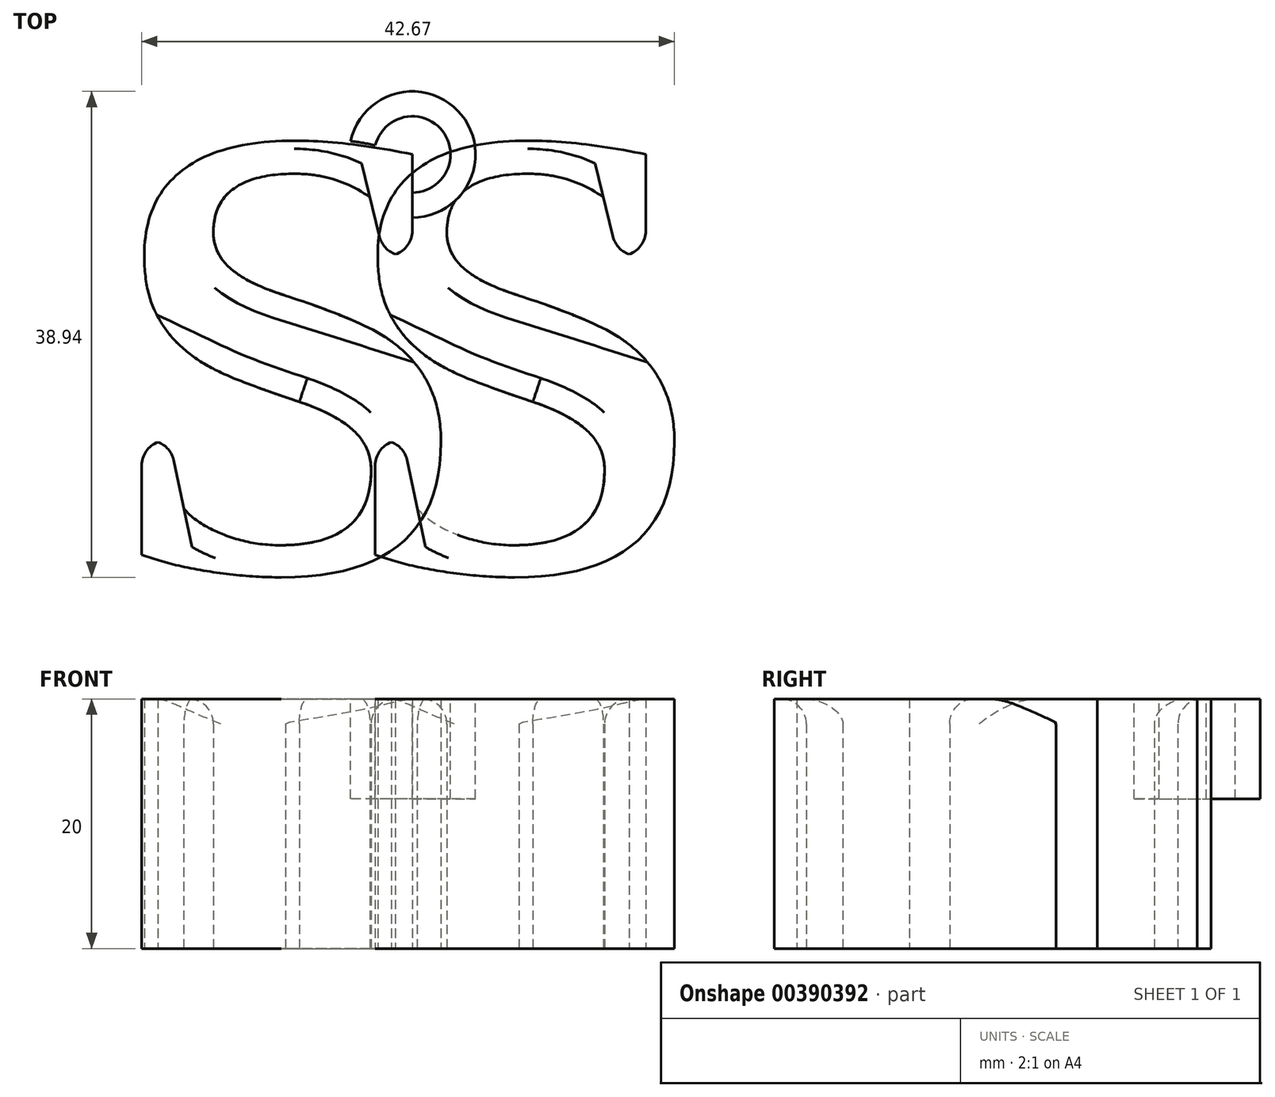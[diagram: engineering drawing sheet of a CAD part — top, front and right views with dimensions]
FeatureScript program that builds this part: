
annotation { "Feature Type Name" : "Feature", "Feature Type Description" : "" }
export const myFeature = defineFeature(function(context is Context, id is Id, definition is map)
    precondition{}
    {
        {
            var Q0;
            Q0=qCreatedBy(makeId("Top.planeOp"),FACE);
            var sketch = newSketch(context, id + "F0", { "sketchPlane" : qUnion([Q0])});
            skText(sketch, "E0", { "text": "S", "fontName": "Tinos-Bold.ttf"});
            const initialGuessF0  = {"E0": [0, -0.03748, 1, 0, 0.03748]};
            skSetInitialGuess(sketch, initialGuessF0);
            skSolve(sketch);
        }
        {
            var Q0;
            Q0=makeQuery(id+"F0.imprint","IMPRINT",FACE,{"disambiguationData":[TD([[makeQuery(id+"F0.imprint","IMPRINT",EDGE,{"derivedFrom":sQuery(id+"F0.wireOp",EDGE,"E0.sketch_text.stroke-0")}),-1.0]])]});
            extrude(context, id + "F1", {"entities" : qUnion([Q0]), "depth" : 20 * mm});
        }
        {
            var Q0;
            Q0=makeQuery(id+"F1.opExtrude","CAP_EDGE",EDGE,{"disambiguationData":[OSD([sQuery(id+"F0.wireOp",EDGE,"E0.sketch_text.stroke-6")])],"isStart":false});
            var Q1;
            Q1=makeQuery(id+"F1.opExtrude","CAP_EDGE",EDGE,{"disambiguationData":[OSD([sQuery(id+"F0.wireOp",EDGE,"E0.sketch_text.stroke-4")])],"isStart":false});
            var Q2;
            Q2=makeQuery(id+"F1.opExtrude","SWEPT_EDGE",EDGE,{"disambiguationData":[OSD([sQuery(id+"F0.wireOp",EDGE,"E0.sketch_text.stroke-4"),sQuery(id+"F0.wireOp",EDGE,"E0.sketch_text.stroke-5")])]});
            var Q3;
            Q3=makeQuery(id+"F1.opExtrude","SWEPT_EDGE",EDGE,{"disambiguationData":[OSD([sQuery(id+"F0.wireOp",EDGE,"E0.sketch_text.stroke-2"),sQuery(id+"F0.wireOp",EDGE,"E0.sketch_text.stroke-3")])]});
            var Q4;
            Q4=makeQuery(id+"F1.opExtrude","SWEPT_EDGE",EDGE,{"disambiguationData":[OSD([sQuery(id+"F0.wireOp",EDGE,"E0.sketch_text.stroke-7"),sQuery(id+"F0.wireOp",EDGE,"E0.sketch_text.stroke-8")])]});
            var Q5;
            Q5=makeQuery(id+"F1.opExtrude","SWEPT_EDGE",EDGE,{"disambiguationData":[OSD([sQuery(id+"F0.wireOp",EDGE,"E0.sketch_text.stroke-0"),sQuery(id+"F0.wireOp",EDGE,"E0.sketch_text.stroke-15")])]});
            var Q6;
            Q6=makeQuery(id+"F1.opExtrude","SWEPT_EDGE",EDGE,{"disambiguationData":[OSD([sQuery(id+"F0.wireOp",EDGE,"E0.sketch_text.stroke-10"),sQuery(id+"F0.wireOp",EDGE,"E0.sketch_text.stroke-11")])]});
            var Q7;
            Q7=makeQuery(id+"F1.opExtrude","SWEPT_EDGE",EDGE,{"disambiguationData":[OSD([sQuery(id+"F0.wireOp",EDGE,"E0.sketch_text.stroke-5"),sQuery(id+"F0.wireOp",EDGE,"E0.sketch_text.stroke-6")])]});
            var Q8;
            Q8=makeQuery(id+"F1.opExtrude","CAP_EDGE",EDGE,{"disambiguationData":[OSD([sQuery(id+"F0.wireOp",EDGE,"E0.sketch_text.stroke-5")])],"isStart":false});
            var Q9;
            Q9=makeQuery(id+"F1.opExtrude","CAP_EDGE",EDGE,{"disambiguationData":[OSD([sQuery(id+"F0.wireOp",EDGE,"E0.sketch_text.stroke-17")])],"isStart":false});
            fillet(context, id + "F2", {"entities" : qUnion([Q0, Q1, Q2, Q3, Q4, Q5, Q6, Q7, Q8, Q9]), "radius" : 2 * mm, "tangentPropagation" : true, "allowEdgeOverflow" : false});
        }
        {
            var Q0;
            Q0=makeQuery(id+"F1.opExtrude","CAP_FACE",FACE,{"disambiguationData":[OSD([sQuery(id+"F0.wireOp",EDGE,"E0.sketch_text.stroke-0"),sQuery(id+"F0.wireOp",EDGE,"E0.sketch_text.stroke-1"),sQuery(id+"F0.wireOp",EDGE,"E0.sketch_text.stroke-2"),sQuery(id+"F0.wireOp",EDGE,"E0.sketch_text.stroke-3"),sQuery(id+"F0.wireOp",EDGE,"E0.sketch_text.stroke-4"),sQuery(id+"F0.wireOp",EDGE,"E0.sketch_text.stroke-5"),sQuery(id+"F0.wireOp",EDGE,"E0.sketch_text.stroke-6"),sQuery(id+"F0.wireOp",EDGE,"E0.sketch_text.stroke-7"),sQuery(id+"F0.wireOp",EDGE,"E0.sketch_text.stroke-8"),sQuery(id+"F0.wireOp",EDGE,"E0.sketch_text.stroke-9"),sQuery(id+"F0.wireOp",EDGE,"E0.sketch_text.stroke-10"),sQuery(id+"F0.wireOp",EDGE,"E0.sketch_text.stroke-11"),sQuery(id+"F0.wireOp",EDGE,"E0.sketch_text.stroke-12"),sQuery(id+"F0.wireOp",EDGE,"E0.sketch_text.stroke-13"),sQuery(id+"F0.wireOp",EDGE,"E0.sketch_text.stroke-14"),sQuery(id+"F0.wireOp",EDGE,"E0.sketch_text.stroke-15"),sQuery(id+"F0.wireOp",EDGE,"E0.sketch_text.stroke-16"),sQuery(id+"F0.wireOp",EDGE,"E0.sketch_text.stroke-17"),sQuery(id+"F0.wireOp",EDGE,"E0.sketch_text.stroke-18"),sQuery(id+"F0.wireOp",EDGE,"E0.sketch_text.stroke-19"),sQuery(id+"F0.wireOp",EDGE,"E0.sketch_text.stroke-20"),sQuery(id+"F0.wireOp",EDGE,"E0.sketch_text.stroke-21"),sQuery(id+"F0.wireOp",EDGE,"E0.sketch_text.stroke-22"),sQuery(id+"F0.wireOp",EDGE,"E0.sketch_text.stroke-23"),sQuery(id+"F0.wireOp",EDGE,"E0.sketch_text.stroke-24"),sQuery(id+"F0.wireOp",EDGE,"E0.sketch_text.stroke-25"),sQuery(id+"F0.wireOp",EDGE,"E0.sketch_text.stroke-26"),sQuery(id+"F0.wireOp",EDGE,"E0.sketch_text.stroke-27"),sQuery(id+"F0.wireOp",EDGE,"E0.sketch_text.stroke-28")])],"isStart":false});
            var sketch = newSketch(context, id + "F3", { "sketchPlane" : qUnion([Q0])});
            skFitSpline(sketch, "E1.0", {"points": [v(15, -3) * mm, v(19.27, -3) * mm, v(24.45, -4.1) * mm]});
            skFitSpline(sketch, "E2.0", {"points": [v(6.04, -5.36) * mm, v(9.1, -3) * mm, v(15, -3) * mm]});
            skLineSegment(sketch, "E3.0", {"start": v(21.82, -10.7) * mm, "end": v(20.4, -4.83) * mm});
            skPoint(sketch, "E4.0", {"position": v(22.28, -11.56) * mm});
            skPoint(sketch, "E5.0", {"position": v(24.08, -11.38) * mm});
            skPoint(sketch, "E6.0", {"position": v(24.45, -7.16) * mm});
            skFitSpline(sketch, "E7.0", {"points": [v(15, -3.65) * mm, v(15.46, -3.65) * mm, v(16.4, -3.7) * mm, v(18.23, -3.98) * mm, v(19.55, -4.42) * mm, v(20.4, -4.83) * mm]});
            skFitSpline(sketch, "E8.0", {"points": [v(9.05, -5.17) * mm, v(9.48, -4.87) * mm, v(10.4, -4.39) * mm, v(11.9, -3.93) * mm, v(13.44, -3.7) * mm, v(14.48, -3.65) * mm, v(15, -3.65) * mm]});
            skCircle(sketch, "E9", {"center": v(24.45, -4.1) * mm, "radius": 3.06 * mm});
            skCircle(sketch, "E10.0", {"center": v(24.45, -4.1) * mm, "radius": 5.06 * mm});
            skSolve(sketch);
        }
        {
            var Q0;
            Q0=makeQuery(id+"F1.opExtrude","SWEPT_BODY",BODY,{"disambiguationData":[OSD([sQuery(id+"F0.wireOp",EDGE,"E0.sketch_text.stroke-0"),sQuery(id+"F0.wireOp",EDGE,"E0.sketch_text.stroke-1"),sQuery(id+"F0.wireOp",EDGE,"E0.sketch_text.stroke-2"),sQuery(id+"F0.wireOp",EDGE,"E0.sketch_text.stroke-3"),sQuery(id+"F0.wireOp",EDGE,"E0.sketch_text.stroke-4"),sQuery(id+"F0.wireOp",EDGE,"E0.sketch_text.stroke-5"),sQuery(id+"F0.wireOp",EDGE,"E0.sketch_text.stroke-6"),sQuery(id+"F0.wireOp",EDGE,"E0.sketch_text.stroke-7"),sQuery(id+"F0.wireOp",EDGE,"E0.sketch_text.stroke-8"),sQuery(id+"F0.wireOp",EDGE,"E0.sketch_text.stroke-9"),sQuery(id+"F0.wireOp",EDGE,"E0.sketch_text.stroke-10"),sQuery(id+"F0.wireOp",EDGE,"E0.sketch_text.stroke-11"),sQuery(id+"F0.wireOp",EDGE,"E0.sketch_text.stroke-12"),sQuery(id+"F0.wireOp",EDGE,"E0.sketch_text.stroke-13"),sQuery(id+"F0.wireOp",EDGE,"E0.sketch_text.stroke-14"),sQuery(id+"F0.wireOp",EDGE,"E0.sketch_text.stroke-15"),sQuery(id+"F0.wireOp",EDGE,"E0.sketch_text.stroke-16"),sQuery(id+"F0.wireOp",EDGE,"E0.sketch_text.stroke-17"),sQuery(id+"F0.wireOp",EDGE,"E0.sketch_text.stroke-18"),sQuery(id+"F0.wireOp",EDGE,"E0.sketch_text.stroke-19"),sQuery(id+"F0.wireOp",EDGE,"E0.sketch_text.stroke-20"),sQuery(id+"F0.wireOp",EDGE,"E0.sketch_text.stroke-21"),sQuery(id+"F0.wireOp",EDGE,"E0.sketch_text.stroke-22"),sQuery(id+"F0.wireOp",EDGE,"E0.sketch_text.stroke-23"),sQuery(id+"F0.wireOp",EDGE,"E0.sketch_text.stroke-24"),sQuery(id+"F0.wireOp",EDGE,"E0.sketch_text.stroke-25"),sQuery(id+"F0.wireOp",EDGE,"E0.sketch_text.stroke-26"),sQuery(id+"F0.wireOp",EDGE,"E0.sketch_text.stroke-27"),sQuery(id+"F0.wireOp",EDGE,"E0.sketch_text.stroke-28")])]});
            transform(context, id + "F4", {"entities" : qUnion([Q0]), "transformType" : TransformType.TRANSLATION_3D, "dx" : 18.7 * mm, "dy" : 0 * mm, "dz" : 0 * mm, "makeCopy" : true});
        }
        {
            var Q0;
            {var subQ0=sQuery(id+"F3.wireOp",EDGE,"E10.0");var subQ1=sQuery(id+"F3.wireOp",EDGE,"E1.0");var subQ2=makeQuery(id+"F3.imprint","INTERSECT",VERTEX,{"derivedFrom":[subQ1,subQ0]});Q0=makeQuery(id+"F3.imprint","IMPRINT",FACE,{"disambiguationData":[TD([[makeQuery(id+"F3.imprint","IMPRINT",EDGE,{"disambiguationData":[TD([[subQ2,-1.0]])],"derivedFrom":subQ1}),1.0]])]});}
            extrude(context, id + "F5", {"entities" : qUnion([Q0]), "oppositeDirection" : true, "depth" : 8 * mm});
        }
    });
